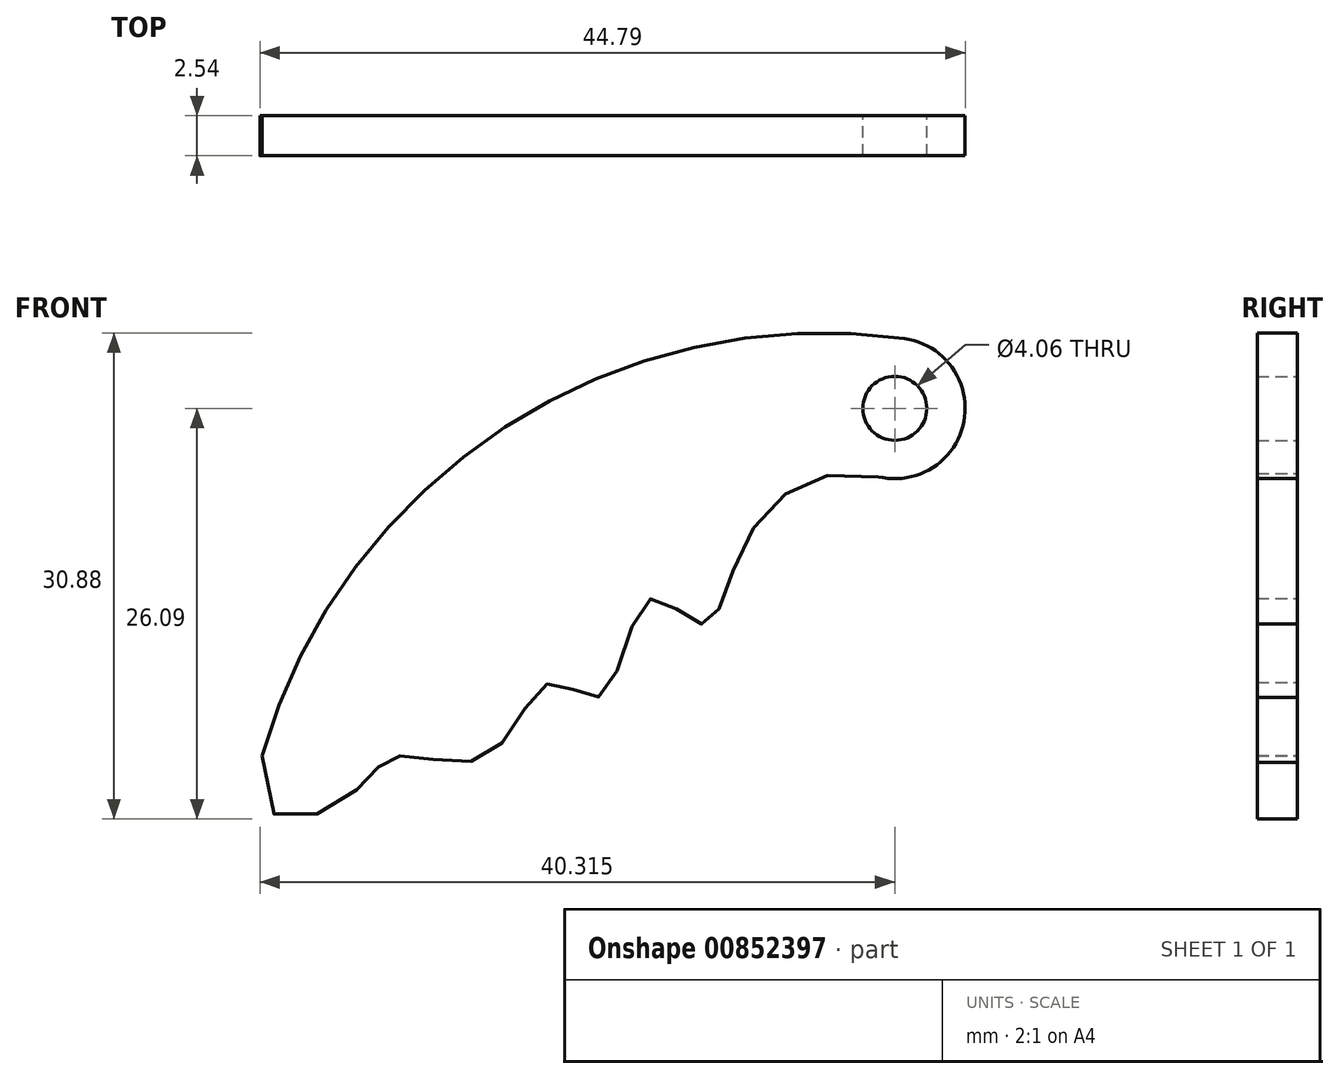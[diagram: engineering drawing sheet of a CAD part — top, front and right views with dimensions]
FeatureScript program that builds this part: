
annotation { "Feature Type Name" : "Feature", "Feature Type Description" : "" }
export const myFeature = defineFeature(function(context is Context, id is Id, definition is map)
    precondition{}
    {
        {
            var Q0;
            Q0=qCreatedBy(makeId("Front.planeOp"),FACE);
            var sketch = newSketch(context, id + "F0", { "sketchPlane" : qUnion([Q0])});
            skCircle(sketch, "E0", {"center": v(6.03, 1.84) * mm, "radius": 2.54 * mm});
            skArc(sketch, "E1.0", {"start": v(4.73, -3.6) * mm, "mid": v(11.52, 0.8) * mm, "end": v(6.81, 7.37) * mm});
            skArc(sketch, "E2", {"start": v(6.81, 7.37) * mm, "mid": v(-24.9, 0.34) * mm, "end": v(-44.21, -25.78) * mm});
            skFitSpline(sketch, "E3", {"points": [v(-44.21, -25.78) * mm, v(-37.63, -29.22) * mm, v(-33.5, -25.78) * mm, v(-26.37, -25.78) * mm, v(-21.29, -19.96) * mm, v(-17.29, -21) * mm, v(-13.43, -13.32) * mm, v(-9.22, -15.29) * mm, v(-5.75, -8.63) * mm, v(4.73, -3.6) * mm], "startDerivative": vector(-28.43, -179.11) * mm, "endDerivative": vector(99.51, -23.88) * mm});
            skSolve(sketch);
        }
        {
            var Q0;
            Q0=qSketchRegion(id+"F0",true);
            extrude(context, id + "F1", {"entities" : qUnion([Q0]), "depth" : 3.17 * mm});
        }
        {
            var Q0;
            Q0=makeQuery(id+"F1.opExtrude","SWEPT_BODY",BODY,{"disambiguationData":[OSD([sQuery(id+"F0.wireOp",EDGE,"E0"),sQuery(id+"F0.wireOp",EDGE,"E1.0"),sQuery(id+"F0.wireOp",EDGE,"E2"),sQuery(id+"F0.wireOp",EDGE,"E3")])]});
            var Q1;
            Q1=qCreatedBy(makeId("Origin.pointOp"),VERTEX);
            transform(context, id + "F2", {"entities" : qUnion([Q0]), "transformType" : TransformType.SCALE_UNIFORMLY, "scale" : 0.8, "scalePoint" : qUnion([Q1]), "makeCopy" : false});
        }
    });
